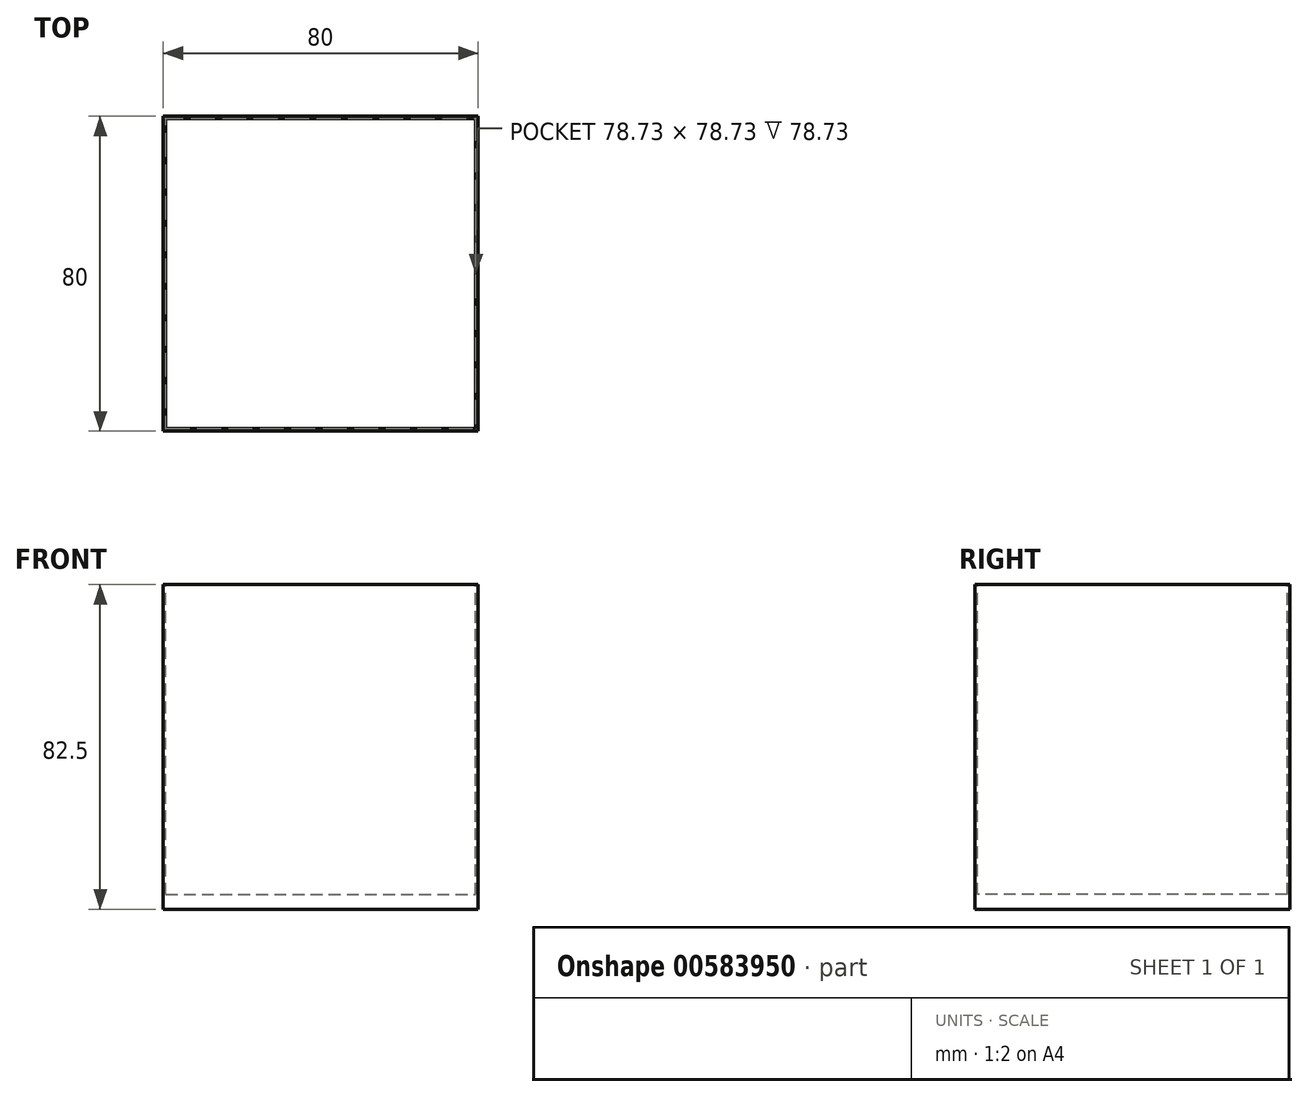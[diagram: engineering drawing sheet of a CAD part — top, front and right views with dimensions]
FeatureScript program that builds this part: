
annotation { "Feature Type Name" : "Feature", "Feature Type Description" : "" }
export const myFeature = defineFeature(function(context is Context, id is Id, definition is map)
    precondition{}
    {
        {
            var Q0;
            Q0=qCreatedBy(makeId("Front.planeOp"),FACE);
            var sketch = newSketch(context, id + "F0", { "sketchPlane" : qUnion([Q0])});
            skLineSegment(sketch, "E0.bottom", {"start": v(-40, 40.42) * mm, "end": v(40, 40.42) * mm});
            skLineSegment(sketch, "E0.top", {"start": v(-40, -42.08) * mm, "end": v(40, -42.08) * mm});
            skLineSegment(sketch, "E0.left", {"start": v(-40, 40.42) * mm, "end": v(-40, -42.08) * mm});
            skLineSegment(sketch, "E0.right", {"start": v(40, 40.42) * mm, "end": v(40, -42.08) * mm});
            skSolve(sketch);
        }
        {
            var Q0;
            Q0=makeQuery(id+"F0.imprint","IMPRINT",FACE,{"disambiguationData":[TD([[makeQuery(id+"F0.imprint","IMPRINT",EDGE,{"derivedFrom":sQuery(id+"F0.wireOp",EDGE,"E0.bottom")}),-1.0]])]});
            extrude(context, id + "F1", {"entities" : qUnion([Q0]), "endBound" : BoundingType.SYMMETRIC, "depth" : 80 * mm, "offsetDistance" : 25.4 * mm});
        }
        {
            var Q0;
            Q0=makeQuery(id+"F1.opExtrude","SWEPT_FACE",FACE,{"disambiguationData":[OSD([sQuery(id+"F0.wireOp",EDGE,"E0.bottom")])]});
            var sketch = newSketch(context, id + "F2", { "sketchPlane" : qUnion([Q0])});
            skLineSegment(sketch, "E1.bottom", {"start": v(-39.36, 39.37) * mm, "end": v(39.37, 39.37) * mm});
            skLineSegment(sketch, "E1.top", {"start": v(-39.37, -39.37) * mm, "end": v(39.36, -39.37) * mm});
            skLineSegment(sketch, "E1.left", {"start": v(-39.36, 39.37) * mm, "end": v(-39.37, -39.36) * mm});
            skLineSegment(sketch, "E1.right", {"start": v(39.37, 39.37) * mm, "end": v(39.36, -39.36) * mm});
            skPoint(sketch, "E1.middle", {"position": v(0, 0) * mm});
            skSolve(sketch);
        }
        {
            var Q0;
            Q0=makeQuery(id+"F2.imprint","IMPRINT",FACE,{"disambiguationData":[TD([[makeQuery(id+"F2.imprint","IMPRINT",EDGE,{"derivedFrom":sQuery(id+"F2.wireOp",EDGE,"E1.bottom")}),-1.0]])]});
            extrude(context, id + "F3", {"entities" : qUnion([Q0]), "operationType" : NewBodyOperationType.REMOVE, "oppositeDirection" : true, "depth" : 78.73 * mm, "offsetDistance" : 25.4 * mm});
        }
    });
